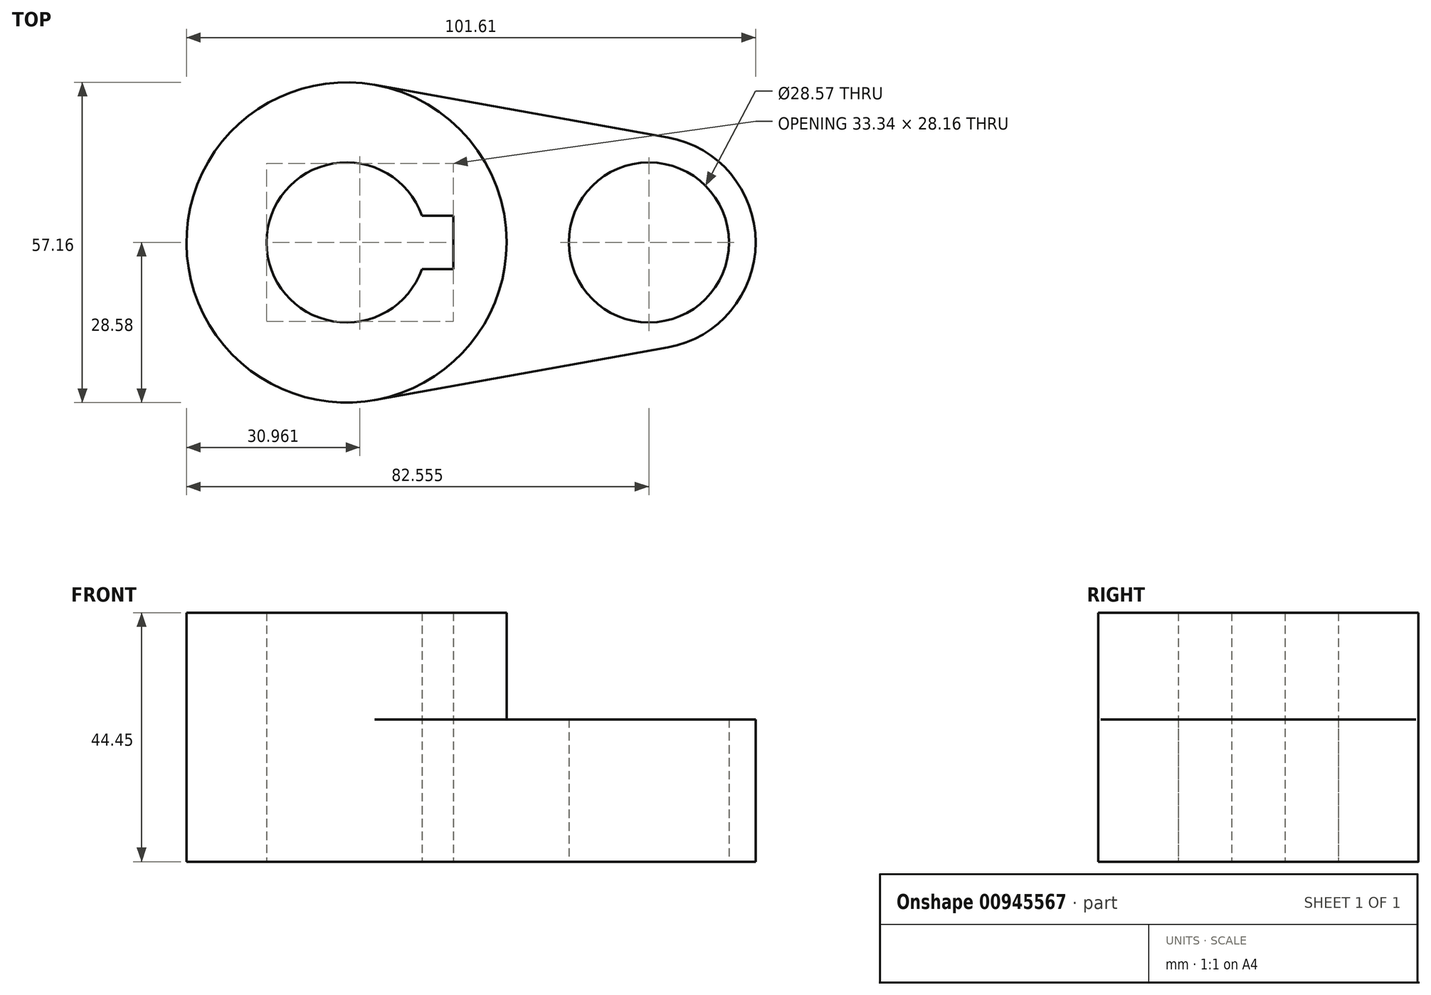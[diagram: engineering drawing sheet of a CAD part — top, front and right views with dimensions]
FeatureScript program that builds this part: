
annotation { "Feature Type Name" : "Feature", "Feature Type Description" : "" }
export const myFeature = defineFeature(function(context is Context, id is Id, definition is map)
    precondition{}
    {
        {
            var Q0;
            Q0=qCreatedBy(makeId("Top.planeOp"),FACE);
            var sketch = newSketch(context, id + "F0", { "sketchPlane" : qUnion([Q0])});
            skCircle(sketch, "E0", {"center": v(0, 0) * mm, "radius": 28.58 * mm});
            skCircle(sketch, "E1", {"center": v(53.98, 0) * mm, "radius": 19.05 * mm});
            skLineSegment(sketch, "E2", {"start": v(5.04, 28.13) * mm, "end": v(57.34, 18.75) * mm});
            skLineSegment(sketch, "E3", {"start": v(5.04, -28.13) * mm, "end": v(57.34, -18.75) * mm});
            skCircle(sketch, "E4", {"center": v(0, 0) * mm, "radius": 14.29 * mm});
            skCircle(sketch, "E5", {"center": v(53.98, 0) * mm, "radius": 14.29 * mm});
            skLineSegment(sketch, "E6.bottom", {"start": v(-19.05, 4.76) * mm, "end": v(19.05, 4.76) * mm});
            skLineSegment(sketch, "E6.top", {"start": v(-19.05, -4.76) * mm, "end": v(19.05, -4.76) * mm});
            skLineSegment(sketch, "E6.left", {"start": v(-19.05, 4.76) * mm, "end": v(-19.05, -4.76) * mm});
            skLineSegment(sketch, "E6.right", {"start": v(19.05, 4.76) * mm, "end": v(19.05, -4.76) * mm});
            skSolve(sketch);
        }
        {
            var Q0;
            {var subQ5=sQuery(id+"F0.wireOp",EDGE,"E6.left");Q0=makeQuery(id+"F0.imprint","IMPRINT",FACE,{"disambiguationData":[TD([[makeQuery(id+"F0.imprint","IMPRINT",EDGE,{"derivedFrom":subQ5}),1.0]])]});}
            var Q1;
            {var subQ0=sQuery(id+"F0.wireOp",EDGE,"E2");Q1=makeQuery(id+"F0.imprint","IMPRINT",FACE,{"disambiguationData":[TD([[makeQuery(id+"F0.imprint","IMPRINT",EDGE,{"derivedFrom":subQ0}),-1.0]])]});}
            var Q2;
            {var subQ7=sQuery(id+"F0.wireOp",EDGE,"E6.left");Q2=makeQuery(id+"F0.imprint","IMPRINT",FACE,{"disambiguationData":[TD([[makeQuery(id+"F0.imprint","IMPRINT",EDGE,{"derivedFrom":subQ7}),-1.0]])]});}
            var Q3;
            Q3=makeQuery(id+"F0.imprint","IMPRINT",FACE,{"disambiguationData":[TD([[makeQuery(id+"F0.imprint","IMPRINT",EDGE,{"derivedFrom":sQuery(id+"F0.wireOp",EDGE,"E5")}),-1.0]])]});
            extrude(context, id + "F1", {"entities" : qUnion([Q0, Q1, Q2, Q3]), "depth" : 25.4 * mm, "offsetDistance" : 25.4 * mm});
        }
        {
            var Q0;
            {var subQ7=sQuery(id+"F0.wireOp",EDGE,"E6.left");Q0=makeQuery(id+"F0.imprint","IMPRINT",FACE,{"disambiguationData":[TD([[makeQuery(id+"F0.imprint","IMPRINT",EDGE,{"derivedFrom":subQ7}),-1.0]])]});}
            var Q1;
            {var subQ5=sQuery(id+"F0.wireOp",EDGE,"E6.left");Q1=makeQuery(id+"F0.imprint","IMPRINT",FACE,{"disambiguationData":[TD([[makeQuery(id+"F0.imprint","IMPRINT",EDGE,{"derivedFrom":subQ5}),1.0]])]});}
            extrude(context, id + "F2", {"entities" : qUnion([Q0, Q1]), "operationType" : NewBodyOperationType.ADD, "depth" : 44.45 * mm, "offsetDistance" : 25.4 * mm});
        }
    });
